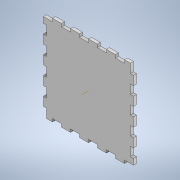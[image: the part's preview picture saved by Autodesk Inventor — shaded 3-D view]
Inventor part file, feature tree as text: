
AUTODESK INVENTOR PART (.ipt)
format: ipt  version: 2021 (Build 250183000, 183)  size: 311,296 bytes
history: native  units: mm
features: sketch x5, extrude x4, pattern_linear x2, pattern_circular x2, projected_geometry x2, other x1
ambient origin geometry x8: Origin, YZ Plane, XZ Plane, XY Plane, X Axis, Y Axis, Z Axis, Center Point
bodies: Solid1 (feature_tree)
feature tree (16):
  extrude  "Extrusion1"  Depth=120.0mm
  extrude  "Extrusion2"  Depth=60.0mm
  pattern_linear  "side_top"  Spacing1=12.0mm  [1 undecoded]
  extrude  "Extrusion3"  Depth=4.0mm
  pattern_circular  "side_bottom"  [2 undecoded]
  pattern_linear  "side_left"  Count1=5  [1 undecoded]
  pattern_circular  "side_right"  [2 undecoded]
  extrude  "Extrusion5"  Depth=4.0mm TaperAngle=0.0deg
  sketch  "Sketch7"  dims[d17=0.0mm d18=12.0mm d19=4.0mm d20=0.0mm d21=50.0mm d23=24.0mm d24=10.0mm d26=0.0mm d28=4.0mm d29=0.0mm d46=20.0mm d47=360.0deg d49=4.0mm d50=12.0mm d51=0.0mm d52=0.0mm d53=50.0mm d55=24.0mm d56=20.0mm d57=360.0deg d59=0.11mm d60=4.0mm d61=0.0mm]
  sketch  "Sketch1"  dims[d0=120.0mm d1=120.0mm]
  sketch  "Sketch3"  dims[d2=60.0mm d3=60.0mm]
  sketch  "Sketch4"  dims[d4=4.0mm]
  other  "Work Axis2"
  sketch  "Sketch6"  dims[d5=0.0mm]
  projected_geometry  "Projected Loop1"
  projected_geometry  "Projected Loop2"
note: 6 required parameter values undecoded (feature->parameter linkage not recoverable at this tier; creation-order binding heuristic only, values carry confidence <= 0.55)
